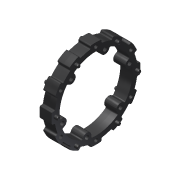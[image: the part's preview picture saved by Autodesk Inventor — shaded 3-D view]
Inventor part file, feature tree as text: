
AUTODESK INVENTOR PART (.ipt)
format: ipt  version: 2013 (Build 170138000, 138)  size: 688,640 bytes
history: native  units: in
note: dims shown in document units (in); Inventor stores cm internally (conversion verified against a paired STEP export)
features: fillet x1, other x1, imported_body x1
ambient origin geometry x8: Origin, YZ Plane, XZ Plane, XY Plane, X Axis, Y Axis, Z Axis, Center Point
feature tree (3):
  fillet  "Fillet3"  [1 undecoded]
  other  "217-2588-003 Rev11"
  imported_body  "Base1"
note: 1 required parameter value undecoded (feature->parameter linkage not recoverable at this tier; creation-order binding heuristic only, values carry confidence <= 0.55)
